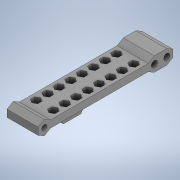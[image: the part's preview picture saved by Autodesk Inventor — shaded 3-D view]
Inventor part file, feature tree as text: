
AUTODESK INVENTOR PART (.ipt)
format: ipt  version: 2020 (Build 240168000, 168)  size: 462,848 bytes
history: native  units: in
note: dims shown in document units (in); Inventor stores cm internally (conversion verified against a paired STEP export)
features: sketch x7, extrude x6, projected_geometry x4, plane x2, mirror x1
ambient origin geometry x8: Origin, YZ Plane, XZ Plane, XY Plane, X Axis, Y Axis, Z Axis, Center Point
bodies: Solid1 (feature_tree)
feature tree (20):
  extrude  "Extrusion1"  Depth=3.4256in
  plane  "Work Plane1"
  extrude  "Extrusion2"  Depth=0.7874in
  sketch  "Sketch4"  dims[d4=0.0in d5=0.0827in]
  extrude  "Extrusion4"  Depth=0.0827in
  plane  "Work Plane2"
  extrude  "Extrusion6"  Depth=3.1106in
  mirror  "Mirror2"
  extrude  "Extrusion7"  Depth=0.315in
  extrude  "Extrusion8"  Depth=0.2362in
  sketch  "Sketch1"  dims[d0=0.1818in d1=3.4256in]
  sketch  "Sketch2"  dims[d2=0.1339in d3=0.7874in]
  sketch  "Sketch5"  dims[d6=0.7874in d7=0.0in d28=3.1106in]
  sketch  "Sketch7"  dims[d29=0.315in d31=0.315in]
  projected_geometry  "Projected Loop7"
  projected_geometry  "Projected Loop8"
  sketch  "Sketch8"  dims[d33=0.1575in d34=0.2362in]
  projected_geometry  "Projected Loop9"
  sketch  "Sketch10"  dims[d35=0.0in d38=0.315in d39=0.2756in d40=-0.3092in d41=0.0787in d42=0.0787in d43=0.0787in d44=3.1496in d46=0.2913in d47=0.3937in d49=0.3937in d51=3.1496in d53=0.2913in d54=0.3937in d56=0.3937in d58=0.0in d59=0.0in d60=150.0deg d61=0.1339in d63=1.1811in d64=0.1575in d65=0.0in d66=0.126in]
  projected_geometry  "Projected Loop10"
